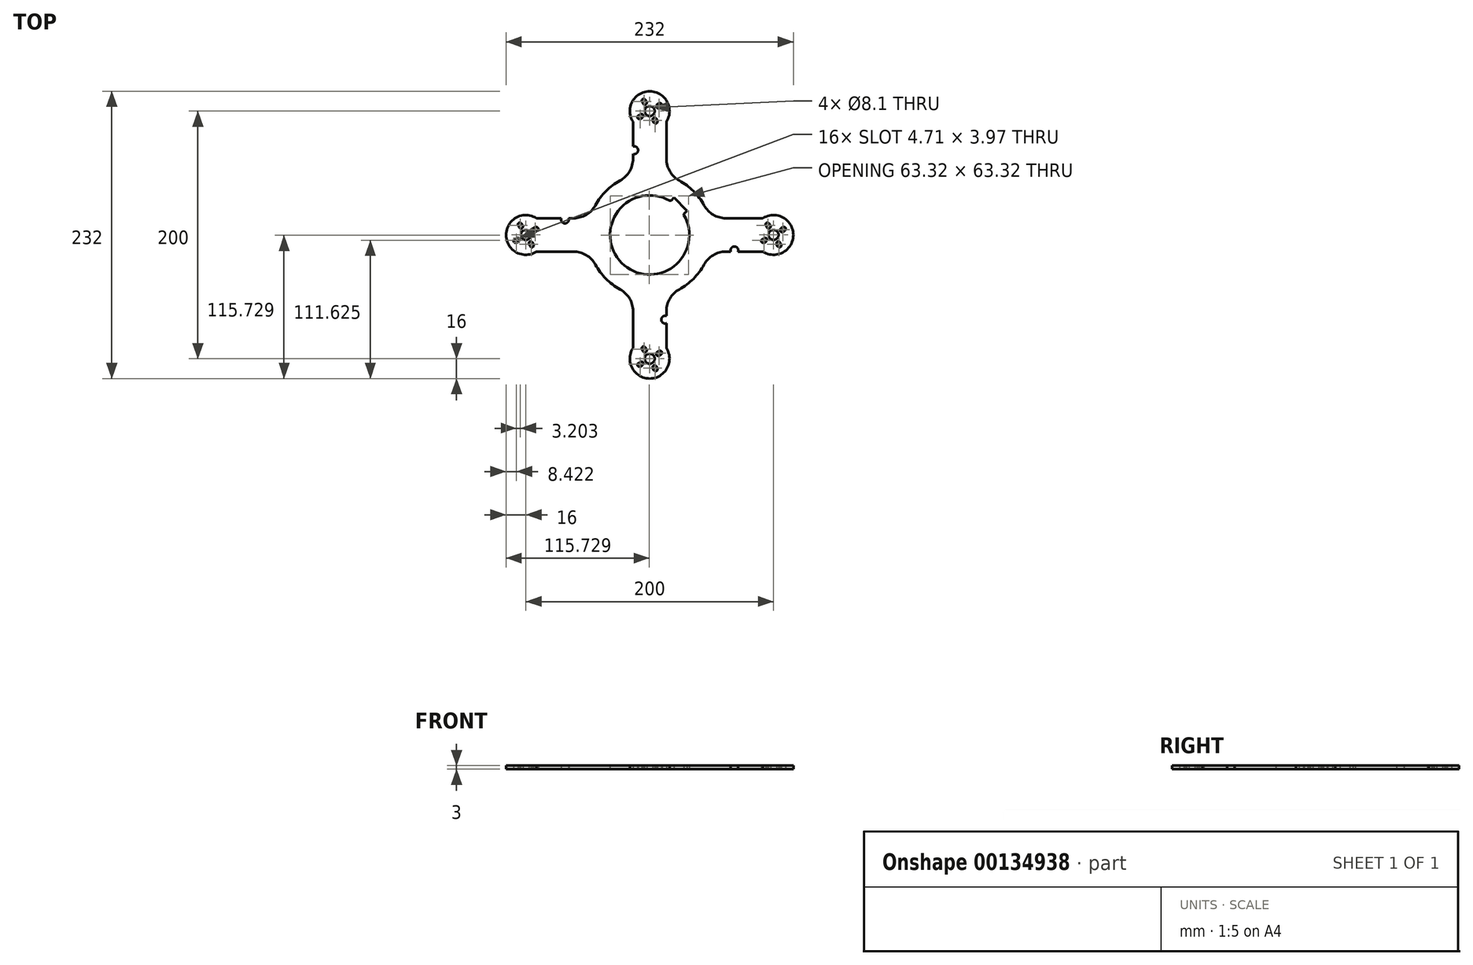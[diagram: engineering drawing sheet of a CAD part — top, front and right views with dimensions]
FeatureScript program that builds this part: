
annotation { "Feature Type Name" : "Feature", "Feature Type Description" : "" }
export const myFeature = defineFeature(function(context is Context, id is Id, definition is map)
    precondition{}
    {
        {
            var Q0;
            Q0=qCreatedBy(makeId("Top.planeOp"),FACE);
            var sketch = newSketch(context, id + "F0", { "sketchPlane" : qUnion([Q0])});
            skArc(sketch, "E0", {"start": v(16.04, 27.7) * mm, "mid": v(-22.63, -22.63) * mm, "end": v(27.7, 16.04) * mm});
            skArc(sketch, "E1", {"start": v(91.41, -13.5) * mm, "mid": v(116, 0) * mm, "end": v(91.41, 13.5) * mm});
            skArc(sketch, "E2.0.startCap", {"start": v(97.42, 7.46) * mm, "mid": v(96.88, 5.41) * mm, "end": v(94.83, 5.96) * mm});
            skArc(sketch, "E2.0.endCap", {"start": v(93.83, 7.7) * mm, "mid": v(94.38, 9.74) * mm, "end": v(96.42, 9.2) * mm});
            skLineSegment(sketch, "E2.0.left", {"start": v(94.83, 5.96) * mm, "end": v(93.83, 7.7) * mm});
            skLineSegment(sketch, "E2.0.right", {"start": v(97.42, 7.46) * mm, "end": v(96.42, 9.2) * mm});
            skCircle(sketch, "E3", {"center": v(100, 0) * mm, "radius": 4.05 * mm});
            skLineSegment(sketch, "E4", {"start": v(100, 0) * mm, "end": v(95.12, 8.44) * mm, "construction": true});
            skLineSegment(sketch, "E5.1.0", {"start": v(105.96, 5.17) * mm, "end": v(107.7, 6.17) * mm});
            skLineSegment(sketch, "E5.1.1", {"start": v(107.46, 2.58) * mm, "end": v(109.2, 3.58) * mm});
            skArc(sketch, "E5.1.2", {"start": v(107.46, 2.58) * mm, "mid": v(105.41, 3.13) * mm, "end": v(105.96, 5.17) * mm});
            skArc(sketch, "E5.1.3", {"start": v(107.7, 6.17) * mm, "mid": v(109.74, 5.63) * mm, "end": v(109.2, 3.58) * mm});
            skLineSegment(sketch, "E5.2.0", {"start": v(105.17, -5.96) * mm, "end": v(106.17, -7.7) * mm});
            skLineSegment(sketch, "E5.2.1", {"start": v(102.58, -7.46) * mm, "end": v(103.58, -9.2) * mm});
            skArc(sketch, "E5.2.2", {"start": v(102.58, -7.46) * mm, "mid": v(103.13, -5.41) * mm, "end": v(105.17, -5.96) * mm});
            skArc(sketch, "E5.2.3", {"start": v(106.17, -7.7) * mm, "mid": v(105.63, -9.74) * mm, "end": v(103.58, -9.2) * mm});
            skLineSegment(sketch, "E5.3.0", {"start": v(94.04, -5.17) * mm, "end": v(92.3, -6.17) * mm});
            skLineSegment(sketch, "E5.3.1", {"start": v(92.54, -2.58) * mm, "end": v(90.8, -3.58) * mm});
            skArc(sketch, "E5.3.2", {"start": v(92.54, -2.58) * mm, "mid": v(94.59, -3.13) * mm, "end": v(94.04, -5.17) * mm});
            skArc(sketch, "E5.3.3", {"start": v(92.3, -6.17) * mm, "mid": v(90.26, -5.63) * mm, "end": v(90.8, -3.58) * mm});
            skLineSegment(sketch, "E5.anchor1", {"start": v(100, 0) * mm, "end": v(96.12, 6.71) * mm, "construction": true});
            skLineSegment(sketch, "E5.anchor2", {"start": v(100, 0) * mm, "end": v(93.29, -3.88) * mm, "construction": true});
            skLineSegment(sketch, "E6", {"start": v(91.41, -13.5) * mm, "end": v(91.41, 13.5) * mm, "construction": true});
            skArc(sketch, "E7", {"start": v(43.9, 23.93) * mm, "mid": v(35.36, 35.36) * mm, "end": v(23.93, 43.9) * mm});
            skArc(sketch, "E8.trimOffspring", {"start": v(-23.93, 43.9) * mm, "mid": v(-35.36, 35.36) * mm, "end": v(-43.9, 23.93) * mm});
            skArc(sketch, "E9.trimOffspring", {"start": v(-43.9, -23.93) * mm, "mid": v(-35.36, -35.36) * mm, "end": v(-23.93, -43.9) * mm});
            skArc(sketch, "E10.trimOffspring", {"start": v(23.93, -43.9) * mm, "mid": v(35.36, -35.36) * mm, "end": v(43.9, -23.93) * mm});
            skCircle(sketch, "E11", {"center": v(100, 0) * mm, "radius": 68 * mm, "construction": true});
            skPoint(sketch, "E12.visualSharp", {"position": v(48.14, 13.5) * mm});
            skArc(sketch, "E12.filletArc", {"start": v(43.9, 23.93) * mm, "mid": v(51.25, 16.3) * mm, "end": v(61.46, 13.5) * mm});
            skPoint(sketch, "E13.visualSharp", {"position": v(48.14, -13.5) * mm});
            skArc(sketch, "E13.filletArc", {"start": v(61.46, -13.5) * mm, "mid": v(51.25, -16.3) * mm, "end": v(43.9, -23.93) * mm});
            skLineSegment(sketch, "E14.1.0", {"start": v(13.5, 91.41) * mm, "end": v(13.5, 61.46) * mm});
            skPoint(sketch, "E14.1.1", {"position": v(13.5, 48.14) * mm});
            skPoint(sketch, "E14.1.2", {"position": v(-13.5, 48.14) * mm});
            skArc(sketch, "E14.1.3", {"start": v(13.5, 91.41) * mm, "mid": v(0, 116) * mm, "end": v(-13.5, 91.41) * mm});
            skPoint(sketch, "E14.1.4", {"position": v(0, 100) * mm});
            skLineSegment(sketch, "E14.1.5", {"start": v(-13.5, 65.41) * mm, "end": v(-13.5, 61.46) * mm});
            skPoint(sketch, "E14.1.6", {"position": v(0, 100) * mm});
            skLineSegment(sketch, "E14.1.7", {"start": v(13.5, 91.41) * mm, "end": v(-13.5, 91.41) * mm, "construction": true});
            skLineSegment(sketch, "E14.1.8", {"start": v(-13.5, 91.41) * mm, "end": v(-13.5, 71.41) * mm});
            skArc(sketch, "E14.1.9", {"start": v(-13.5, 65.41) * mm, "mid": v(-9.34, 68.41) * mm, "end": v(-13.5, 71.41) * mm});
            skArc(sketch, "E14.1.10", {"start": v(7.46, 102.58) * mm, "mid": v(5.41, 103.13) * mm, "end": v(5.96, 105.17) * mm});
            skLineSegment(sketch, "E14.1.11", {"start": v(-2.58, 107.46) * mm, "end": v(-3.58, 109.2) * mm});
            skLineSegment(sketch, "E14.1.12", {"start": v(-5.17, 105.96) * mm, "end": v(-6.17, 107.7) * mm});
            skArc(sketch, "E14.1.13", {"start": v(7.7, 106.17) * mm, "mid": v(9.74, 105.63) * mm, "end": v(9.2, 103.58) * mm});
            skArc(sketch, "E14.1.14", {"start": v(-6.17, 107.7) * mm, "mid": v(-5.63, 109.74) * mm, "end": v(-3.58, 109.2) * mm});
            skLineSegment(sketch, "E14.1.15", {"start": v(7.46, 102.58) * mm, "end": v(9.2, 103.58) * mm});
            skLineSegment(sketch, "E14.1.16", {"start": v(5.96, 105.17) * mm, "end": v(7.7, 106.17) * mm});
            skLineSegment(sketch, "E14.1.17", {"start": v(5.17, 94.04) * mm, "end": v(6.17, 92.3) * mm});
            skArc(sketch, "E14.1.18", {"start": v(2.58, 92.54) * mm, "mid": v(3.13, 94.59) * mm, "end": v(5.17, 94.04) * mm});
            skLineSegment(sketch, "E14.1.19", {"start": v(2.58, 92.54) * mm, "end": v(3.58, 90.8) * mm});
            skArc(sketch, "E14.1.20", {"start": v(6.17, 92.3) * mm, "mid": v(5.63, 90.26) * mm, "end": v(3.58, 90.8) * mm});
            skLineSegment(sketch, "E14.1.21", {"start": v(-7.46, 97.42) * mm, "end": v(-9.2, 96.42) * mm});
            skLineSegment(sketch, "E14.1.22", {"start": v(-5.96, 94.83) * mm, "end": v(-7.7, 93.83) * mm});
            skArc(sketch, "E14.1.23", {"start": v(-7.7, 93.83) * mm, "mid": v(-9.74, 94.38) * mm, "end": v(-9.2, 96.42) * mm});
            skLineSegment(sketch, "E14.1.24", {"start": v(0, 100) * mm, "end": v(-8.44, 95.12) * mm, "construction": true});
            skLineSegment(sketch, "E14.1.25", {"start": v(0, 100) * mm, "end": v(3.88, 93.29) * mm, "construction": true});
            skArc(sketch, "E14.1.26", {"start": v(-7.46, 97.42) * mm, "mid": v(-5.41, 96.88) * mm, "end": v(-5.96, 94.83) * mm});
            skCircle(sketch, "E14.1.27", {"center": v(0, 100) * mm, "radius": 4.05 * mm});
            skLineSegment(sketch, "E14.1.28", {"start": v(0, 100) * mm, "end": v(-6.71, 96.13) * mm, "construction": true});
            skArc(sketch, "E14.1.29", {"start": v(-2.58, 107.46) * mm, "mid": v(-3.13, 105.41) * mm, "end": v(-5.17, 105.96) * mm});
            skCircle(sketch, "E14.1.30", {"center": v(0, 100) * mm, "radius": 68 * mm, "construction": true});
            skArc(sketch, "E14.1.31", {"start": v(13.5, 61.46) * mm, "mid": v(16.3, 51.25) * mm, "end": v(23.93, 43.9) * mm});
            skArc(sketch, "E14.1.32", {"start": v(-23.93, 43.9) * mm, "mid": v(-16.3, 51.25) * mm, "end": v(-13.5, 61.46) * mm});
            skLineSegment(sketch, "E14.2.0", {"start": v(-91.41, 13.5) * mm, "end": v(-71.41, 13.5) * mm});
            skPoint(sketch, "E14.2.1", {"position": v(-48.14, 13.5) * mm});
            skPoint(sketch, "E14.2.2", {"position": v(-48.14, -13.5) * mm});
            skArc(sketch, "E14.2.3", {"start": v(-91.41, 13.5) * mm, "mid": v(-116, 0) * mm, "end": v(-91.41, -13.5) * mm});
            skPoint(sketch, "E14.2.4", {"position": v(-100, 0) * mm});
            skLineSegment(sketch, "E14.2.5", {"start": v(-65.41, -13.5) * mm, "end": v(-61.46, -13.5) * mm});
            skPoint(sketch, "E14.2.6", {"position": v(-100, 0) * mm});
            skLineSegment(sketch, "E14.2.7", {"start": v(-91.41, 13.5) * mm, "end": v(-91.41, -13.5) * mm, "construction": true});
            skLineSegment(sketch, "E14.2.8", {"start": v(-91.41, -13.5) * mm, "end": v(-71.41, -13.5) * mm});
            skArc(sketch, "E14.2.10", {"start": v(-102.58, 7.46) * mm, "mid": v(-103.13, 5.41) * mm, "end": v(-105.17, 5.96) * mm});
            skLineSegment(sketch, "E14.2.11", {"start": v(-107.46, -2.58) * mm, "end": v(-109.2, -3.58) * mm});
            skLineSegment(sketch, "E14.2.12", {"start": v(-105.96, -5.17) * mm, "end": v(-107.7, -6.17) * mm});
            skArc(sketch, "E14.2.13", {"start": v(-106.17, 7.7) * mm, "mid": v(-105.63, 9.74) * mm, "end": v(-103.58, 9.2) * mm});
            skArc(sketch, "E14.2.14", {"start": v(-107.7, -6.17) * mm, "mid": v(-109.74, -5.63) * mm, "end": v(-109.2, -3.58) * mm});
            skLineSegment(sketch, "E14.2.15", {"start": v(-102.58, 7.46) * mm, "end": v(-103.58, 9.2) * mm});
            skLineSegment(sketch, "E14.2.16", {"start": v(-105.17, 5.96) * mm, "end": v(-106.17, 7.7) * mm});
            skLineSegment(sketch, "E14.2.17", {"start": v(-94.04, 5.17) * mm, "end": v(-92.3, 6.17) * mm});
            skArc(sketch, "E14.2.18", {"start": v(-92.54, 2.58) * mm, "mid": v(-94.59, 3.13) * mm, "end": v(-94.04, 5.17) * mm});
            skLineSegment(sketch, "E14.2.19", {"start": v(-92.54, 2.58) * mm, "end": v(-90.8, 3.58) * mm});
            skArc(sketch, "E14.2.20", {"start": v(-92.3, 6.17) * mm, "mid": v(-90.26, 5.63) * mm, "end": v(-90.8, 3.58) * mm});
            skLineSegment(sketch, "E14.2.21", {"start": v(-97.42, -7.46) * mm, "end": v(-96.42, -9.2) * mm});
            skLineSegment(sketch, "E14.2.22", {"start": v(-94.83, -5.96) * mm, "end": v(-93.83, -7.7) * mm});
            skArc(sketch, "E14.2.23", {"start": v(-93.83, -7.7) * mm, "mid": v(-94.38, -9.74) * mm, "end": v(-96.42, -9.2) * mm});
            skLineSegment(sketch, "E14.2.24", {"start": v(-100, 0) * mm, "end": v(-95.12, -8.44) * mm, "construction": true});
            skLineSegment(sketch, "E14.2.25", {"start": v(-100, 0) * mm, "end": v(-93.29, 3.88) * mm, "construction": true});
            skArc(sketch, "E14.2.26", {"start": v(-97.42, -7.46) * mm, "mid": v(-96.88, -5.41) * mm, "end": v(-94.83, -5.96) * mm});
            skCircle(sketch, "E14.2.27", {"center": v(-100, 0) * mm, "radius": 4.05 * mm});
            skLineSegment(sketch, "E14.2.28", {"start": v(-100, 0) * mm, "end": v(-96.12, -6.71) * mm, "construction": true});
            skArc(sketch, "E14.2.29", {"start": v(-107.46, -2.58) * mm, "mid": v(-105.41, -3.13) * mm, "end": v(-105.96, -5.17) * mm});
            skCircle(sketch, "E14.2.30", {"center": v(-100, 0) * mm, "radius": 68 * mm, "construction": true});
            skArc(sketch, "E14.2.31", {"start": v(-61.46, 13.5) * mm, "mid": v(-51.25, 16.3) * mm, "end": v(-43.9, 23.93) * mm});
            skArc(sketch, "E14.2.32", {"start": v(-43.9, -23.93) * mm, "mid": v(-51.25, -16.3) * mm, "end": v(-61.46, -13.5) * mm});
            skLineSegment(sketch, "E14.3.0", {"start": v(-13.5, -91.41) * mm, "end": v(-13.5, -61.46) * mm});
            skPoint(sketch, "E14.3.1", {"position": v(-13.5, -48.14) * mm});
            skPoint(sketch, "E14.3.2", {"position": v(13.5, -48.14) * mm});
            skArc(sketch, "E14.3.3", {"start": v(-13.5, -91.41) * mm, "mid": v(0, -116) * mm, "end": v(13.5, -91.41) * mm});
            skPoint(sketch, "E14.3.4", {"position": v(0, -100) * mm});
            skLineSegment(sketch, "E14.3.5", {"start": v(13.5, -65.41) * mm, "end": v(13.5, -61.46) * mm});
            skPoint(sketch, "E14.3.6", {"position": v(0, -100) * mm});
            skLineSegment(sketch, "E14.3.7", {"start": v(-13.5, -91.41) * mm, "end": v(13.5, -91.41) * mm, "construction": true});
            skLineSegment(sketch, "E14.3.8", {"start": v(13.5, -91.41) * mm, "end": v(13.5, -71.41) * mm});
            skArc(sketch, "E14.3.9", {"start": v(13.5, -65.41) * mm, "mid": v(9.34, -68.41) * mm, "end": v(13.5, -71.41) * mm});
            skArc(sketch, "E14.3.10", {"start": v(-7.46, -102.58) * mm, "mid": v(-5.41, -103.13) * mm, "end": v(-5.96, -105.17) * mm});
            skLineSegment(sketch, "E14.3.11", {"start": v(2.58, -107.46) * mm, "end": v(3.58, -109.2) * mm});
            skLineSegment(sketch, "E14.3.12", {"start": v(5.17, -105.96) * mm, "end": v(6.17, -107.7) * mm});
            skArc(sketch, "E14.3.13", {"start": v(-7.7, -106.17) * mm, "mid": v(-9.74, -105.63) * mm, "end": v(-9.2, -103.58) * mm});
            skArc(sketch, "E14.3.14", {"start": v(6.17, -107.7) * mm, "mid": v(5.63, -109.74) * mm, "end": v(3.58, -109.2) * mm});
            skLineSegment(sketch, "E14.3.15", {"start": v(-7.46, -102.58) * mm, "end": v(-9.2, -103.58) * mm});
            skLineSegment(sketch, "E14.3.16", {"start": v(-5.96, -105.17) * mm, "end": v(-7.7, -106.17) * mm});
            skLineSegment(sketch, "E14.3.17", {"start": v(-5.17, -94.04) * mm, "end": v(-6.17, -92.3) * mm});
            skArc(sketch, "E14.3.18", {"start": v(-2.58, -92.54) * mm, "mid": v(-3.13, -94.59) * mm, "end": v(-5.17, -94.04) * mm});
            skLineSegment(sketch, "E14.3.19", {"start": v(-2.58, -92.54) * mm, "end": v(-3.58, -90.8) * mm});
            skArc(sketch, "E14.3.20", {"start": v(-6.17, -92.3) * mm, "mid": v(-5.63, -90.26) * mm, "end": v(-3.58, -90.8) * mm});
            skLineSegment(sketch, "E14.3.21", {"start": v(7.46, -97.42) * mm, "end": v(9.2, -96.42) * mm});
            skLineSegment(sketch, "E14.3.22", {"start": v(5.96, -94.83) * mm, "end": v(7.7, -93.83) * mm});
            skArc(sketch, "E14.3.23", {"start": v(7.7, -93.83) * mm, "mid": v(9.74, -94.38) * mm, "end": v(9.2, -96.42) * mm});
            skLineSegment(sketch, "E14.3.24", {"start": v(0, -100) * mm, "end": v(8.44, -95.13) * mm, "construction": true});
            skLineSegment(sketch, "E14.3.25", {"start": v(0, -100) * mm, "end": v(-3.88, -93.29) * mm, "construction": true});
            skArc(sketch, "E14.3.26", {"start": v(7.46, -97.42) * mm, "mid": v(5.41, -96.88) * mm, "end": v(5.96, -94.83) * mm});
            skCircle(sketch, "E14.3.27", {"center": v(0, -100) * mm, "radius": 4.05 * mm});
            skLineSegment(sketch, "E14.3.28", {"start": v(0, -100) * mm, "end": v(6.71, -96.13) * mm, "construction": true});
            skArc(sketch, "E14.3.29", {"start": v(2.58, -107.46) * mm, "mid": v(3.13, -105.41) * mm, "end": v(5.17, -105.96) * mm});
            skCircle(sketch, "E14.3.30", {"center": v(0, -100) * mm, "radius": 68 * mm, "construction": true});
            skArc(sketch, "E14.3.31", {"start": v(-13.5, -61.46) * mm, "mid": v(-16.3, -51.25) * mm, "end": v(-23.93, -43.9) * mm});
            skArc(sketch, "E14.3.32", {"start": v(23.93, -43.9) * mm, "mid": v(16.3, -51.25) * mm, "end": v(13.5, -61.46) * mm});
            skCircle(sketch, "E15", {"center": v(0, 0) * mm, "radius": 100 * mm, "construction": true});
            skLineSegment(sketch, "E16", {"start": v(0, 0) * mm, "end": v(35.36, 35.36) * mm, "construction": true});
            skLineSegment(sketch, "E17", {"start": v(17.24, 27.85) * mm, "end": v(19.52, 30.13) * mm});
            skLineSegment(sketch, "E18", {"start": v(19.52, 30.13) * mm, "end": v(30.13, 19.52) * mm});
            skLineSegment(sketch, "E19", {"start": v(30.13, 19.52) * mm, "end": v(27.85, 17.24) * mm});
            skPoint(sketch, "E20.visualSharp", {"position": v(16.7, 27.3) * mm});
            skArc(sketch, "E20.filletArc", {"start": v(16.04, 27.7) * mm, "mid": v(16.67, 27.57) * mm, "end": v(17.24, 27.85) * mm});
            skPoint(sketch, "E21.visualSharp", {"position": v(27.3, 16.7) * mm});
            skArc(sketch, "E21.filletArc", {"start": v(27.85, 17.24) * mm, "mid": v(27.57, 16.67) * mm, "end": v(27.7, 16.04) * mm});
            skCircle(sketch, "E22", {"center": v(100, 0) * mm, "radius": 7.75 * mm, "construction": true});
            skCircle(sketch, "E23", {"center": v(100, 0) * mm, "radius": 9.75 * mm, "construction": true});
            skArc(sketch, "E24.MirrorCS", {"start": v(65.41, -13.5) * mm, "mid": v(68.41, -9.34) * mm, "end": v(71.41, -13.5) * mm});
            skArc(sketch, "E25.MirrorCS", {"start": v(-65.41, 13.5) * mm, "mid": v(-68.41, 9.34) * mm, "end": v(-71.41, 13.5) * mm});
            skLineSegment(sketch, "E26", {"start": v(0, 0) * mm, "end": v(0, -100) * mm, "construction": true});
            skLineSegment(sketch, "E27.trimOffspring", {"start": v(-65.41, 13.5) * mm, "end": v(-61.46, 13.5) * mm});
            skLineSegment(sketch, "E28", {"start": v(-71.41, -13.5) * mm, "end": v(-65.41, -13.5) * mm});
            skLineSegment(sketch, "E29", {"start": v(61.46, 13.5) * mm, "end": v(71.41, 13.5) * mm});
            skLineSegment(sketch, "E30", {"start": v(61.46, -13.5) * mm, "end": v(65.41, -13.5) * mm});
            skLineSegment(sketch, "E31", {"start": v(71.41, 13.5) * mm, "end": v(91.41, 13.5) * mm});
            skLineSegment(sketch, "E32", {"start": v(71.41, -13.5) * mm, "end": v(91.41, -13.5) * mm});
            skSolve(sketch);
        }
        {
            var Q0;
            Q0=makeQuery(id+"F0.imprint","IMPRINT",FACE,{"disambiguationData":[TD([[makeQuery(id+"F0.imprint","IMPRINT",EDGE,{"derivedFrom":sQuery(id+"F0.wireOp",EDGE,"E0")}),-1.0]])]});
            extrude(context, id + "F1", {"entities" : qUnion([Q0]), "depth" : 3 * mm});
        }
    });
